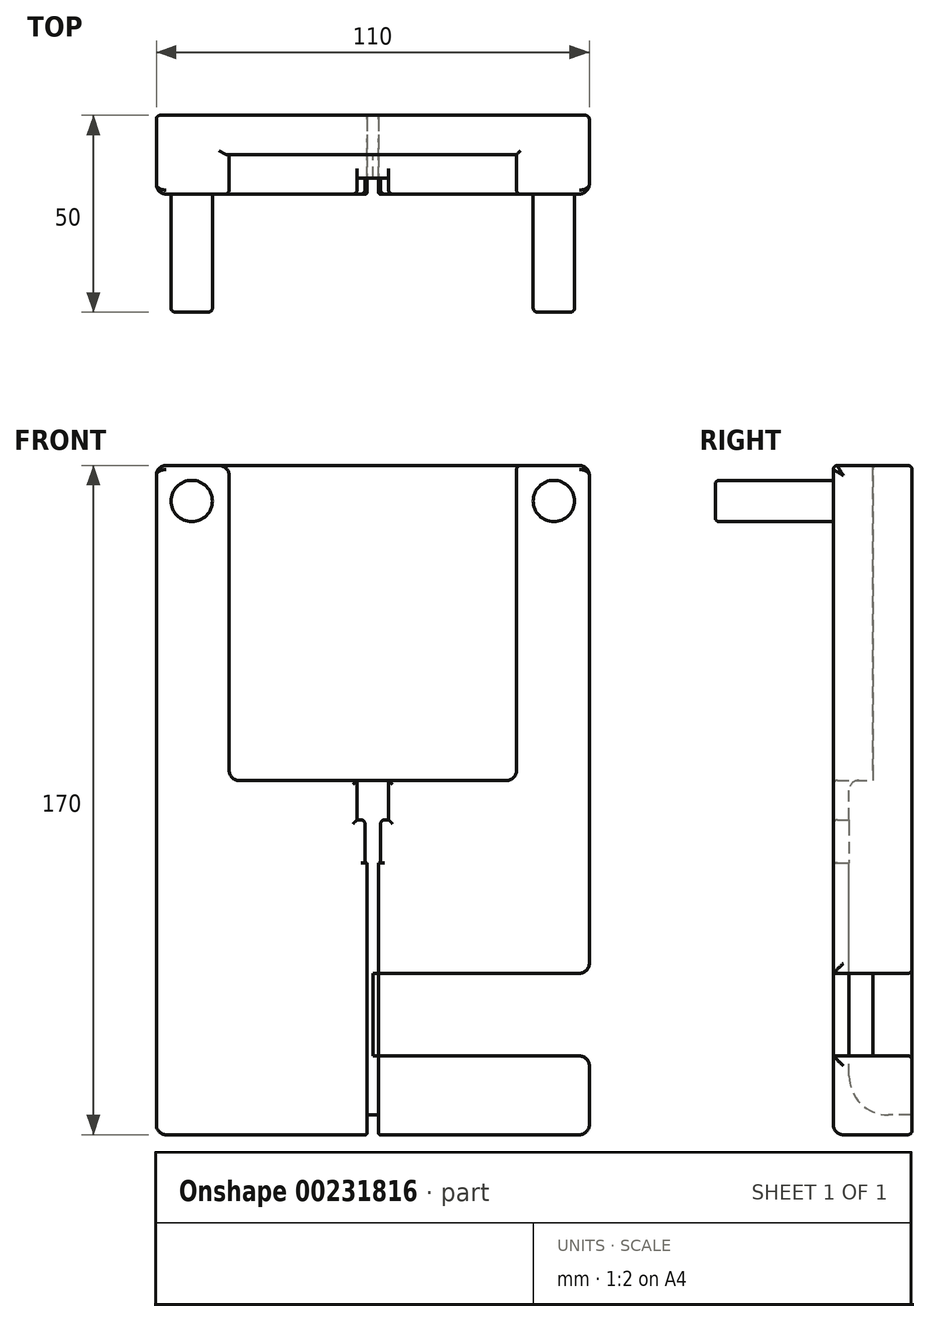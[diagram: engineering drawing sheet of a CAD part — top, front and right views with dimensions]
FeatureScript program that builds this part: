
annotation { "Feature Type Name" : "Feature", "Feature Type Description" : "" }
export const myFeature = defineFeature(function(context is Context, id is Id, definition is map)
    precondition{}
    {
        {
            var Q0;
            Q0=qCreatedBy(makeId("Front.planeOp"),FACE);
            var sketch = newSketch(context, id + "F0", { "sketchPlane" : qUnion([Q0])});
            skLineSegment(sketch, "E0.bottom", {"start": v(0, 0) * mm, "end": v(110, 0) * mm});
            skLineSegment(sketch, "E0.top", {"start": v(0, 170) * mm, "end": v(110, 170) * mm});
            skLineSegment(sketch, "E0.left", {"start": v(0, 0) * mm, "end": v(0, 170) * mm});
            skLineSegment(sketch, "E0.right", {"start": v(110, 0) * mm, "end": v(110, 170) * mm});
            skLineSegment(sketch, "E1", {"start": v(18.5, 170) * mm, "end": v(18.5, 90) * mm});
            skLineSegment(sketch, "E2", {"start": v(18.5, 90) * mm, "end": v(91.5, 90) * mm});
            skLineSegment(sketch, "E3", {"start": v(91.5, 90) * mm, "end": v(91.5, 170) * mm});
            skLineSegment(sketch, "E4", {"start": v(110, 41) * mm, "end": v(55, 41) * mm});
            skLineSegment(sketch, "E5", {"start": v(55, 41) * mm, "end": v(55, 20) * mm});
            skLineSegment(sketch, "E6", {"start": v(55, 20) * mm, "end": v(110, 20) * mm});
            skLineSegment(sketch, "E7", {"start": v(18.5, 90) * mm, "end": v(55, 90) * mm});
            skLineSegment(sketch, "E8", {"start": v(55, 90) * mm, "end": v(55, 170) * mm, "construction": true});
            skLineSegment(sketch, "E9", {"start": v(55, 170) * mm, "end": v(0, 170) * mm});
            skCircle(sketch, "E10", {"center": v(101, 161) * mm, "radius": 5.25 * mm});
            skCircle(sketch, "E11", {"center": v(9, 161) * mm, "radius": 5.25 * mm});
            skLineSegment(sketch, "E12", {"start": v(55, 90) * mm, "end": v(55, 80) * mm, "construction": true});
            skLineSegment(sketch, "E13", {"start": v(55, 80) * mm, "end": v(51, 80) * mm});
            skLineSegment(sketch, "E14", {"start": v(51, 80) * mm, "end": v(51, 90) * mm});
            skLineSegment(sketch, "E15", {"start": v(55, 80) * mm, "end": v(59, 80) * mm});
            skLineSegment(sketch, "E16", {"start": v(59, 80) * mm, "end": v(59, 90) * mm});
            skLineSegment(sketch, "E17", {"start": v(55, 80) * mm, "end": v(55, 69) * mm, "construction": true});
            skLineSegment(sketch, "E18", {"start": v(55, 69) * mm, "end": v(55, 0) * mm, "construction": true});
            skLineSegment(sketch, "E19", {"start": v(55, 69) * mm, "end": v(53, 69) * mm});
            skLineSegment(sketch, "E20", {"start": v(53, 69) * mm, "end": v(53, 80) * mm});
            skLineSegment(sketch, "E21", {"start": v(53, 80) * mm, "end": v(57, 80) * mm});
            skLineSegment(sketch, "E22", {"start": v(57, 80) * mm, "end": v(57, 69) * mm});
            skLineSegment(sketch, "E23", {"start": v(57, 69) * mm, "end": v(55, 69) * mm});
            skLineSegment(sketch, "E24", {"start": v(55, 0) * mm, "end": v(53.5, 0) * mm, "construction": true});
            skLineSegment(sketch, "E25", {"start": v(53.5, 0) * mm, "end": v(53.5, 69) * mm});
            skLineSegment(sketch, "E26", {"start": v(55, 0) * mm, "end": v(56.5, 0) * mm, "construction": true});
            skLineSegment(sketch, "E27", {"start": v(56.5, 0) * mm, "end": v(56.5, 69) * mm});
            skLineSegment(sketch, "E28", {"start": v(53.5, 0) * mm, "end": v(56.5, 0) * mm});
            skLineSegment(sketch, "E29", {"start": v(53.5, 0) * mm, "end": v(53.5, 5) * mm});
            skLineSegment(sketch, "E30", {"start": v(53.5, 5) * mm, "end": v(56.5, 5) * mm});
            skLineSegment(sketch, "E31", {"start": v(56.5, 5) * mm, "end": v(56.5, 0) * mm});
            skSolve(sketch);
        }
        {
            var Q0;
            {var subQ3=sQuery(id+"F0.wireOp",EDGE,"E0.left");Q0=makeQuery(id+"F0.imprint","IMPRINT",FACE,{"disambiguationData":[TD([[makeQuery(id+"F0.imprint","IMPRINT",EDGE,{"derivedFrom":subQ3}),-1.0]])]});}
            var Q1;
            Q1=makeQuery(id+"F0.imprint","IMPRINT",FACE,{"disambiguationData":[TD([[makeQuery(id+"F0.imprint","IMPRINT",EDGE,{"derivedFrom":sQuery(id+"F0.wireOp",EDGE,"E13")}),-1.0]])]});
            var Q2;
            {var subQ0=sQuery(id+"F0.wireOp",EDGE,"E20");Q2=makeQuery(id+"F0.imprint","IMPRINT",FACE,{"disambiguationData":[TD([[makeQuery(id+"F0.imprint","IMPRINT",EDGE,{"derivedFrom":subQ0}),-1.0]])]});}
            var Q3;
            {var subQ5=sQuery(id+"F0.wireOp",EDGE,"E5");Q3=makeQuery(id+"F0.imprint","IMPRINT",FACE,{"disambiguationData":[TD([[makeQuery(id+"F0.imprint","IMPRINT",EDGE,{"derivedFrom":subQ5}),-1.0]])]});}
            var Q4;
            {var subQ0=sQuery(id+"F0.wireOp",EDGE,"E0.right");var subQ1=sQuery(id+"F0.wireOp",EDGE,"E0.bottom");var subQ2=makeQuery(id+"F0.imprint","INTERSECT",VERTEX,{"derivedFrom":[subQ1,subQ0]});Q4=makeQuery(id+"F0.imprint","IMPRINT",FACE,{"disambiguationData":[TD([[makeQuery(id+"F0.imprint","IMPRINT",EDGE,{"disambiguationData":[TD([[subQ2,-1.0]])],"derivedFrom":subQ0}),1.0]])]});}
            var Q5;
            {var subQ0=sQuery(id+"F0.wireOp",EDGE,"E5");Q5=makeQuery(id+"F0.imprint","IMPRINT",FACE,{"disambiguationData":[TD([[makeQuery(id+"F0.imprint","IMPRINT",EDGE,{"derivedFrom":subQ0}),1.0]])]});}
            var Q6;
            {var subQ11=sQuery(id+"F0.wireOp",EDGE,"E3");Q6=makeQuery(id+"F0.imprint","IMPRINT",FACE,{"disambiguationData":[TD([[makeQuery(id+"F0.imprint","IMPRINT",EDGE,{"derivedFrom":subQ11}),-1.0]])]});}
            var Q7;
            {var subQ8=sQuery(id+"F0.wireOp",EDGE,"E1");Q7=makeQuery(id+"F0.imprint","IMPRINT",FACE,{"disambiguationData":[TD([[makeQuery(id+"F0.imprint","IMPRINT",EDGE,{"derivedFrom":subQ8}),1.0]])]});}
            var Q8;
            Q8=makeQuery(id+"F0.imprint","IMPRINT",FACE,{"disambiguationData":[TD([[makeQuery(id+"F0.imprint","IMPRINT",EDGE,{"derivedFrom":sQuery(id+"F0.wireOp",EDGE,"E11")}),1.0]])]});
            var Q9;
            Q9=makeQuery(id+"F0.imprint","IMPRINT",FACE,{"disambiguationData":[TD([[makeQuery(id+"F0.imprint","IMPRINT",EDGE,{"derivedFrom":sQuery(id+"F0.wireOp",EDGE,"E10")}),1.0]])]});
            extrude(context, id + "F1", {"entities" : qUnion([Q0, Q1, Q2, Q3, Q4, Q5, Q6, Q7, Q8, Q9]), "oppositeDirection" : true, "depth" : 10 * mm});
        }
        {
            var Q0;
            Q0=makeQuery(id+"F0.imprint","IMPRINT",FACE,{"disambiguationData":[TD([[makeQuery(id+"F0.imprint","IMPRINT",EDGE,{"derivedFrom":sQuery(id+"F0.wireOp",EDGE,"E13")}),-1.0]])]});
            var Q1;
            {var subQ0=sQuery(id+"F0.wireOp",EDGE,"E20");Q1=makeQuery(id+"F0.imprint","IMPRINT",FACE,{"disambiguationData":[TD([[makeQuery(id+"F0.imprint","IMPRINT",EDGE,{"derivedFrom":subQ0}),-1.0]])]});}
            var Q2;
            {var subQ5=sQuery(id+"F0.wireOp",EDGE,"E5");Q2=makeQuery(id+"F0.imprint","IMPRINT",FACE,{"disambiguationData":[TD([[makeQuery(id+"F0.imprint","IMPRINT",EDGE,{"derivedFrom":subQ5}),-1.0]])]});}
            extrude(context, id + "F2", {"entities" : qUnion([Q0, Q1, Q2]), "operationType" : NewBodyOperationType.ADD, "depth" : 6 * mm});
        }
        {
            var Q0;
            {var subQ3=sQuery(id+"F0.wireOp",EDGE,"E0.left");Q0=makeQuery(id+"F0.imprint","IMPRINT",FACE,{"disambiguationData":[TD([[makeQuery(id+"F0.imprint","IMPRINT",EDGE,{"derivedFrom":subQ3}),-1.0]])]});}
            var Q1;
            {var subQ11=sQuery(id+"F0.wireOp",EDGE,"E3");Q1=makeQuery(id+"F0.imprint","IMPRINT",FACE,{"disambiguationData":[TD([[makeQuery(id+"F0.imprint","IMPRINT",EDGE,{"derivedFrom":subQ11}),-1.0]])]});}
            var Q2;
            {var subQ0=sQuery(id+"F0.wireOp",EDGE,"E0.right");var subQ1=sQuery(id+"F0.wireOp",EDGE,"E0.bottom");var subQ2=makeQuery(id+"F0.imprint","INTERSECT",VERTEX,{"derivedFrom":[subQ1,subQ0]});Q2=makeQuery(id+"F0.imprint","IMPRINT",FACE,{"disambiguationData":[TD([[makeQuery(id+"F0.imprint","IMPRINT",EDGE,{"disambiguationData":[TD([[subQ2,-1.0]])],"derivedFrom":subQ0}),1.0]])]});}
            extrude(context, id + "F3", {"entities" : qUnion([Q0, Q1, Q2]), "operationType" : NewBodyOperationType.ADD, "depth" : 10 * mm});
        }
        {
            var Q0;
            Q0=makeQuery(id+"F0.imprint","IMPRINT",FACE,{"disambiguationData":[TD([[makeQuery(id+"F0.imprint","IMPRINT",EDGE,{"derivedFrom":sQuery(id+"F0.wireOp",EDGE,"E11")}),1.0]])]});
            var Q1;
            Q1=makeQuery(id+"F0.imprint","IMPRINT",FACE,{"disambiguationData":[TD([[makeQuery(id+"F0.imprint","IMPRINT",EDGE,{"derivedFrom":sQuery(id+"F0.wireOp",EDGE,"E10")}),1.0]])]});
            extrude(context, id + "F4", {"entities" : qUnion([Q0, Q1]), "operationType" : NewBodyOperationType.ADD, "depth" : 40 * mm});
        }
        {
            var Q0;
            {var subQ0=sQuery(id+"F0.wireOp",EDGE,"E9");var subQ1=sQuery(id+"F0.wireOp",EDGE,"E0.left");Q0=makeQuery(id+"F3.boolean.opBoolean","MERGE",EDGE,{"derivedFrom":[makeQuery(id+"F1.opExtrude","SWEPT_EDGE",EDGE,{"disambiguationData":[OSD([subQ1,subQ0])]}),makeQuery(id+"F3.opExtrude","SWEPT_EDGE",EDGE,{"disambiguationData":[OSD([subQ1,subQ0])]})]});}
            var Q1;
            {var subQ0=sQuery(id+"F0.wireOp",EDGE,"E0.right");var subQ1=sQuery(id+"F0.wireOp",EDGE,"E0.top");Q1=makeQuery(id+"F3.boolean.opBoolean","MERGE",EDGE,{"derivedFrom":[makeQuery(id+"F1.opExtrude","SWEPT_EDGE",EDGE,{"disambiguationData":[OSD([subQ1,subQ0])]}),makeQuery(id+"F3.opExtrude","SWEPT_EDGE",EDGE,{"disambiguationData":[OSD([subQ1,subQ0])]})]});}
            var Q2;
            {var subQ0=sQuery(id+"F0.wireOp",EDGE,"E4");var subQ1=sQuery(id+"F0.wireOp",EDGE,"E0.right");Q2=makeQuery(id+"F3.boolean.opBoolean","MERGE",EDGE,{"derivedFrom":[makeQuery(id+"F1.opExtrude","SWEPT_EDGE",EDGE,{"disambiguationData":[OSD([subQ1,subQ0])]}),makeQuery(id+"F3.opExtrude","SWEPT_EDGE",EDGE,{"disambiguationData":[OSD([subQ1,subQ0])]})]});}
            var Q3;
            {var subQ0=sQuery(id+"F0.wireOp",EDGE,"E6");var subQ1=sQuery(id+"F0.wireOp",EDGE,"E0.right");Q3=makeQuery(id+"F3.boolean.opBoolean","MERGE",EDGE,{"derivedFrom":[makeQuery(id+"F1.opExtrude","SWEPT_EDGE",EDGE,{"disambiguationData":[OSD([subQ1,subQ0])]}),makeQuery(id+"F3.opExtrude","SWEPT_EDGE",EDGE,{"disambiguationData":[OSD([subQ1,subQ0])]})]});}
            var Q4;
            {var subQ0=sQuery(id+"F0.wireOp",EDGE,"E0.right");var subQ1=sQuery(id+"F0.wireOp",EDGE,"E0.bottom");Q4=makeQuery(id+"F3.boolean.opBoolean","MERGE",EDGE,{"derivedFrom":[makeQuery(id+"F1.opExtrude","SWEPT_EDGE",EDGE,{"disambiguationData":[OSD([subQ1,subQ0])]}),makeQuery(id+"F3.opExtrude","SWEPT_EDGE",EDGE,{"disambiguationData":[OSD([subQ1,subQ0])]})]});}
            var Q5;
            {var subQ0=sQuery(id+"F0.wireOp",EDGE,"E0.left");var subQ1=sQuery(id+"F0.wireOp",EDGE,"E0.bottom");Q5=makeQuery(id+"F3.boolean.opBoolean","MERGE",EDGE,{"derivedFrom":[makeQuery(id+"F1.opExtrude","SWEPT_EDGE",EDGE,{"disambiguationData":[OSD([subQ1,subQ0])]}),makeQuery(id+"F3.opExtrude","SWEPT_EDGE",EDGE,{"disambiguationData":[OSD([subQ1,subQ0])]})]});}
            var Q6;
            Q6=makeQuery(id+"F3.opExtrude","CAP_EDGE",EDGE,{"disambiguationData":[OSD([sQuery(id+"F0.wireOp",EDGE,"E0.left")])],"isStart":false});
            var Q7;
            {var subQ0=sQuery(id+"F0.wireOp",EDGE,"E0.right");Q7=makeQuery(id+"F3.opExtrude","CAP_EDGE",EDGE,{"disambiguationData":[OSD([subQ0]),TDD([makeQuery(id+"F0.imprint","IMPRINT",EDGE,{"disambiguationData":[TD([[makeQuery(id+"F0.imprint","INTERSECT",VERTEX,{"derivedFrom":[sQuery(id+"F0.wireOp",EDGE,"E0.top"),subQ0]}),1.0]])],"derivedFrom":subQ0})])],"isStart":false});}
            var Q8;
            {var subQ0=sQuery(id+"F0.wireOp",EDGE,"E0.bottom");Q8=makeQuery(id+"F3.opExtrude","CAP_EDGE",EDGE,{"disambiguationData":[OSD([subQ0]),TDD([makeQuery(id+"F0.imprint","IMPRINT",EDGE,{"disambiguationData":[TD([[makeQuery(id+"F0.imprint","INTERSECT",VERTEX,{"derivedFrom":[subQ0,sQuery(id+"F0.wireOp",EDGE,"E0.right")]}),1.0]])],"derivedFrom":subQ0})])],"isStart":false});}
            var Q9;
            Q9=makeQuery(id+"F3.opExtrude","SWEPT_EDGE",EDGE,{"disambiguationData":[OSD([sQuery(id+"F0.wireOp",EDGE,"E2"),sQuery(id+"F0.wireOp",EDGE,"E3")])]});
            var Q10;
            Q10=makeQuery(id+"F3.opExtrude","SWEPT_EDGE",EDGE,{"disambiguationData":[OSD([sQuery(id+"F0.wireOp",EDGE,"E1"),sQuery(id+"F0.wireOp",EDGE,"E7")])]});
            var Q11;
            Q11=makeQuery(id+"F2.opExtrude","CAP_EDGE",EDGE,{"disambiguationData":[OSD([sQuery(id+"F0.wireOp",EDGE,"E2"),sQuery(id+"F0.wireOp",EDGE,"E7")])],"isStart":false});
            var Q12;
            {var subQ0=sQuery(id+"F0.wireOp",EDGE,"E0.right");Q12=makeQuery(id+"F3.opExtrude","CAP_EDGE",EDGE,{"disambiguationData":[OSD([subQ0]),TDD([makeQuery(id+"F0.imprint","IMPRINT",EDGE,{"disambiguationData":[TD([[makeQuery(id+"F0.imprint","INTERSECT",VERTEX,{"derivedFrom":[sQuery(id+"F0.wireOp",EDGE,"E0.bottom"),subQ0]}),-1.0]])],"derivedFrom":subQ0})])],"isStart":false});}
            var Q13;
            {var subQ0=sQuery(id+"F0.wireOp",EDGE,"E0.bottom");Q13=makeQuery(id+"F3.opExtrude","CAP_EDGE",EDGE,{"disambiguationData":[OSD([subQ0]),TDD([makeQuery(id+"F0.imprint","IMPRINT",EDGE,{"disambiguationData":[TD([[makeQuery(id+"F0.imprint","INTERSECT",VERTEX,{"derivedFrom":[subQ0,sQuery(id+"F0.wireOp",EDGE,"E0.left")]}),-1.0]])],"derivedFrom":subQ0})])],"isStart":false});}
            fillet(context, id + "F5", {"entities" : qUnion([Q0, Q1, Q2, Q3, Q4, Q5, Q6, Q7, Q8, Q9, Q10, Q11, Q12, Q13]), "radius" : 2.5 * mm, "tangentPropagation" : true, "allowEdgeOverflow" : false});
        }
        {
            var Q0;
            Q0=makeQuery(id+"F3.opExtrude","SWEPT_EDGE",EDGE,{"disambiguationData":[OSD([sQuery(id+"F0.wireOp",EDGE,"E13"),sQuery(id+"F0.wireOp",EDGE,"E20"),sQuery(id+"F0.wireOp",EDGE,"E21")])]});
            var Q1;
            Q1=makeQuery(id+"F3.opExtrude","SWEPT_EDGE",EDGE,{"disambiguationData":[OSD([sQuery(id+"F0.wireOp",EDGE,"E15"),sQuery(id+"F0.wireOp",EDGE,"E21"),sQuery(id+"F0.wireOp",EDGE,"E22")])]});
            var Q2;
            Q2=makeQuery(id+"F3.opExtrude","SWEPT_EDGE",EDGE,{"disambiguationData":[OSD([sQuery(id+"F0.wireOp",EDGE,"E1"),sQuery(id+"F0.wireOp",EDGE,"E9")])]});
            var Q3;
            Q3=makeQuery(id+"F1.opExtrude","CAP_EDGE",EDGE,{"disambiguationData":[OSD([sQuery(id+"F0.wireOp",EDGE,"E0.top"),sQuery(id+"F0.wireOp",EDGE,"E9")])],"isStart":true});
            var Q4;
            Q4=makeQuery(id+"F3.opExtrude","SWEPT_EDGE",EDGE,{"disambiguationData":[OSD([sQuery(id+"F0.wireOp",EDGE,"E0.top"),sQuery(id+"F0.wireOp",EDGE,"E3")])]});
            var Q5;
            Q5=makeQuery(id+"F3.opExtrude","CAP_EDGE",EDGE,{"disambiguationData":[OSD([sQuery(id+"F0.wireOp",EDGE,"E0.top")])],"isStart":false});
            var Q6;
            {var subQ0=sQuery(id+"F0.wireOp",EDGE,"E9");var subQ1=sQuery(id+"F0.wireOp",EDGE,"E0.top");Q6=makeQuery(id+"F3.boolean.opBoolean","MERGE",FACE,{"derivedFrom":[makeQuery(id+"F1.opExtrude","SWEPT_FACE",FACE,{"disambiguationData":[OSD([subQ1,subQ0])]}),makeQuery(id+"F3.opExtrude","SWEPT_FACE",FACE,{"disambiguationData":[OSD([subQ1])]}),makeQuery(id+"F3.opExtrude","SWEPT_FACE",FACE,{"disambiguationData":[OSD([subQ0])]})]});}
            var Q7;
            Q7=makeQuery(id+"F3.opExtrude","CAP_EDGE",EDGE,{"disambiguationData":[OSD([sQuery(id+"F0.wireOp",EDGE,"E1")])],"isStart":false});
            var Q8;
            Q8=makeQuery(id+"F3.opExtrude","CAP_EDGE",EDGE,{"disambiguationData":[OSD([sQuery(id+"F0.wireOp",EDGE,"E3")])],"isStart":false});
            var Q9;
            Q9=makeQuery(id+"F3.opExtrude","CAP_EDGE",EDGE,{"disambiguationData":[OSD([sQuery(id+"F0.wireOp",EDGE,"E14")])],"isStart":false});
            var Q10;
            Q10=makeQuery(id+"F3.opExtrude","CAP_EDGE",EDGE,{"disambiguationData":[OSD([sQuery(id+"F0.wireOp",EDGE,"E16")])],"isStart":false});
            var Q11;
            Q11=makeQuery(id+"F3.opExtrude","CAP_EDGE",EDGE,{"disambiguationData":[OSD([sQuery(id+"F0.wireOp",EDGE,"E22")])],"isStart":false});
            var Q12;
            Q12=makeQuery(id+"F3.opExtrude","CAP_EDGE",EDGE,{"disambiguationData":[OSD([sQuery(id+"F0.wireOp",EDGE,"E20")])],"isStart":false});
            var Q13;
            Q13=makeQuery(id+"F3.opExtrude","CAP_EDGE",EDGE,{"disambiguationData":[OSD([sQuery(id+"F0.wireOp",EDGE,"E13")])],"isStart":false});
            var Q14;
            Q14=makeQuery(id+"F3.opExtrude","CAP_EDGE",EDGE,{"disambiguationData":[OSD([sQuery(id+"F0.wireOp",EDGE,"E15")])],"isStart":false});
            var Q15;
            Q15=makeQuery(id+"F3.opExtrude","CAP_EDGE",EDGE,{"disambiguationData":[OSD([sQuery(id+"F0.wireOp",EDGE,"E3")])],"isStart":true});
            var Q16;
            Q16=makeQuery(id+"F1.opExtrude","CAP_EDGE",EDGE,{"disambiguationData":[OSD([sQuery(id+"F0.wireOp",EDGE,"E0.top"),sQuery(id+"F0.wireOp",EDGE,"E9")])],"isStart":false});
            var Q17;
            Q17=makeQuery(id+"F4.opExtrude","CAP_EDGE",EDGE,{"disambiguationData":[OSD([sQuery(id+"F0.wireOp",EDGE,"E11")])],"isStart":false});
            var Q18;
            Q18=makeQuery(id+"F4.opExtrude","CAP_EDGE",EDGE,{"disambiguationData":[OSD([sQuery(id+"F0.wireOp",EDGE,"E10")])],"isStart":false});
            var Q19;
            {var subQ0=sQuery(id+"F0.wireOp",EDGE,"E0.right");Q19=makeQuery(id+"F1.opExtrude","CAP_EDGE",EDGE,{"disambiguationData":[OSD([subQ0]),TDD([makeQuery(id+"F0.imprint","IMPRINT",EDGE,{"disambiguationData":[TD([[makeQuery(id+"F0.imprint","INTERSECT",VERTEX,{"derivedFrom":[sQuery(id+"F0.wireOp",EDGE,"E0.bottom"),subQ0]}),-1.0]])],"derivedFrom":subQ0})])],"isStart":false});}
            fillet(context, id + "F6", {"entities" : qUnion([Q0, Q1, Q2, Q3, Q4, Q5, Q6, Q7, Q8, Q9, Q10, Q11, Q12, Q13, Q14, Q15, Q16, Q17, Q18, Q19]), "radius" : 1 * mm, "tangentPropagation" : true, "allowEdgeOverflow" : false});
        }
        {
            var Q0;
            Q0=makeQuery(id+"F3.opExtrude","CAP_EDGE",EDGE,{"disambiguationData":[OSD([sQuery(id+"F0.wireOp",EDGE,"E25")])],"isStart":false});
            var Q1;
            {var subQ0=sQuery(id+"F0.wireOp",EDGE,"E27");Q1=makeQuery(id+"F3.opExtrude","CAP_EDGE",EDGE,{"disambiguationData":[OSD([subQ0]),TDD([makeQuery(id+"F0.imprint","IMPRINT",EDGE,{"disambiguationData":[TD([[makeQuery(id+"F0.imprint","INTERSECT",VERTEX,{"derivedFrom":[sQuery(id+"F0.wireOp",EDGE,"E23"),subQ0]}),1.0]])],"derivedFrom":subQ0})])],"isStart":false});}
            var Q2;
            {var subQ0=sQuery(id+"F0.wireOp",EDGE,"E27");Q2=makeQuery(id+"F3.opExtrude","CAP_EDGE",EDGE,{"disambiguationData":[OSD([subQ0]),TDD([makeQuery(id+"F0.imprint","IMPRINT",EDGE,{"disambiguationData":[TD([[makeQuery(id+"F0.imprint","INTERSECT",VERTEX,{"derivedFrom":[sQuery(id+"F0.wireOp",EDGE,"E6"),subQ0]}),1.0]])],"derivedFrom":subQ0})])],"isStart":false});}
            var Q3;
            Q3=makeQuery(id+"F3.opExtrude","CAP_EDGE",EDGE,{"disambiguationData":[OSD([sQuery(id+"F0.wireOp",EDGE,"E27"),sQuery(id+"F0.wireOp",EDGE,"E31")])],"isStart":false});
            fillet(context, id + "F7", {"entities" : qUnion([Q0, Q1, Q2, Q3]), "radius" : 0.3 * mm, "tangentPropagation" : true, "allowEdgeOverflow" : false});
        }
        {
            var Q0;
            Q0=makeQuery(id+"F2.opExtrude","CAP_EDGE",EDGE,{"disambiguationData":[OSD([sQuery(id+"F0.wireOp",EDGE,"E30")])],"isStart":false});
            fillet(context, id + "F8", {"entities" : qUnion([Q0]), "radius" : 10 * mm, "tangentPropagation" : true, "allowEdgeOverflow" : false});
        }
    });
